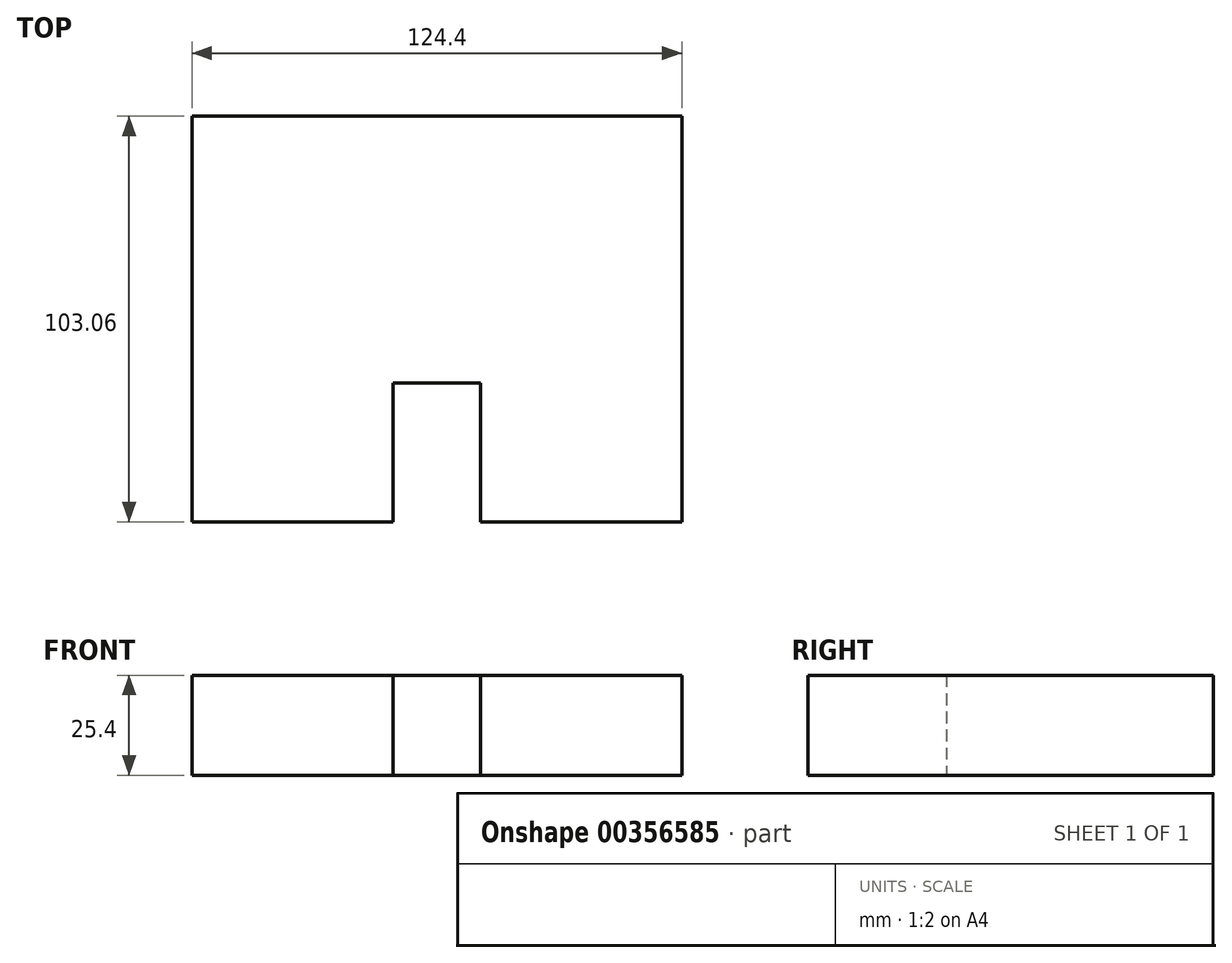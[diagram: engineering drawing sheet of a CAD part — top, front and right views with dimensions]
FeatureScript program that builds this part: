
annotation { "Feature Type Name" : "Feature", "Feature Type Description" : "" }
export const myFeature = defineFeature(function(context is Context, id is Id, definition is map)
    precondition{}
    {
        {
            var Q0;
            Q0=qCreatedBy(makeId("Top.planeOp"),FACE);
            var sketch = newSketch(context, id + "F0", { "sketchPlane" : qUnion([Q0])});
            skLineSegment(sketch, "E0.bottom", {"start": v(62.2, 51.53) * mm, "end": v(-62.2, 51.53) * mm});
            skLineSegment(sketch, "E0.top", {"start": v(62.2, -51.53) * mm, "end": v(-62.2, -51.53) * mm});
            skLineSegment(sketch, "E0.left", {"start": v(62.2, 51.53) * mm, "end": v(62.2, -51.53) * mm});
            skLineSegment(sketch, "E0.right", {"start": v(-62.2, 51.53) * mm, "end": v(-62.2, -51.53) * mm});
            skPoint(sketch, "E0.middle", {"position": v(0, 0) * mm});
            skLineSegment(sketch, "E1.bottom", {"start": v(11.14, -16.25) * mm, "end": v(-11.14, -16.25) * mm});
            skLineSegment(sketch, "E1.top", {"start": v(11.14, -51.53) * mm, "end": v(-11.14, -51.53) * mm});
            skLineSegment(sketch, "E1.left", {"start": v(11.14, -16.25) * mm, "end": v(11.14, -51.53) * mm});
            skLineSegment(sketch, "E1.right", {"start": v(-11.14, -16.25) * mm, "end": v(-11.14, -51.53) * mm});
            skPoint(sketch, "E1.middle", {"position": v(0, -33.89) * mm});
            skSolve(sketch);
        }
        {
            var Q0;
            Q0=makeQuery(id+"F0.imprint","IMPRINT",FACE,{"disambiguationData":[TD([[makeQuery(id+"F0.imprint","IMPRINT",EDGE,{"derivedFrom":sQuery(id+"F0.wireOp",EDGE,"E0.bottom")}),1.0]])]});
            extrude(context, id + "F1", {"entities" : qUnion([Q0]), "depth" : 25.4 * mm});
        }
    });
